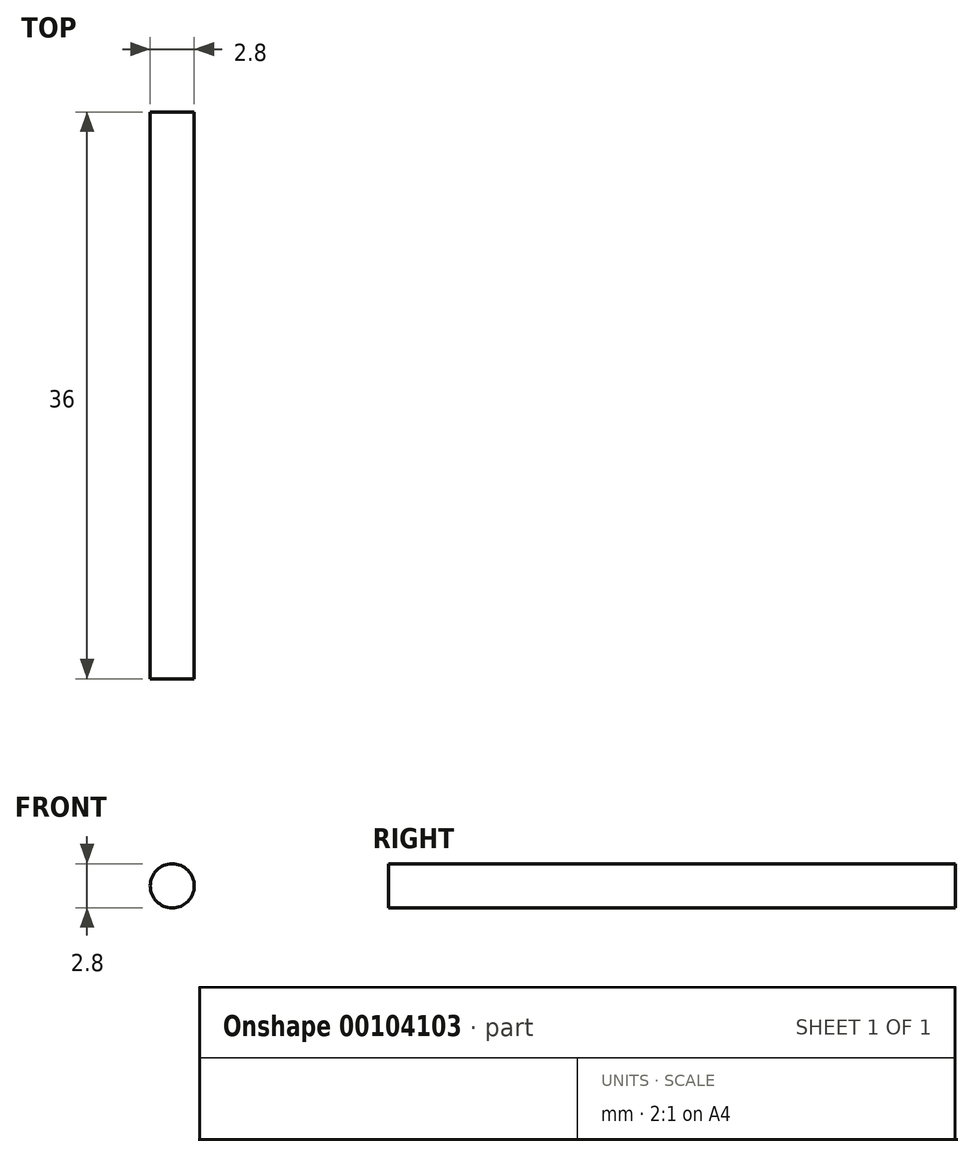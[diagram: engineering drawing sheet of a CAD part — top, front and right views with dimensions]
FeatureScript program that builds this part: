
annotation { "Feature Type Name" : "Feature", "Feature Type Description" : "" }
export const myFeature = defineFeature(function(context is Context, id is Id, definition is map)
    precondition{}
    {
        {
            var Q0;
            Q0=qCreatedBy(makeId("Front.planeOp"),FACE);
            var sketch = newSketch(context, id + "F0", { "sketchPlane" : qUnion([Q0])});
            skCircle(sketch, "E0", {"center": v(0, 0) * mm, "radius": 1.4 * mm});
            skSolve(sketch);
        }
        {
            var Q0;
            Q0=makeQuery(id+"F0.imprint","IMPRINT",FACE,{"disambiguationData":[TD([[makeQuery(id+"F0.imprint","IMPRINT",EDGE,{"derivedFrom":sQuery(id+"F0.wireOp",EDGE,"E0")}),1.0]])]});
            extrude(context, id + "F1", {"entities" : qUnion([Q0]), "depth" : 36 * mm});
        }
    });
